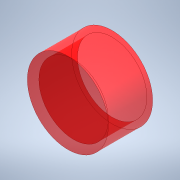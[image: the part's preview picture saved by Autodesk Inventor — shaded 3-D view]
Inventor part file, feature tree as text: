
AUTODESK INVENTOR PART (.ipt)
format: ipt  version: 2022.1 (Build 261234000, 234)  size: 387,584 bytes
history: native  units: mm
features: other x2, sketch x2, extrude x2
ambient origin geometry x8: Origin, YZ Plane, XZ Plane, XY Plane, X Axis, Y Axis, Z Axis, Center Point
bodies: Body1 (feature_tree)
feature tree (6):
  other  "plastic diffuser"
  other  "Твердое тело1"
  sketch  "Эскиз1"
  extrude  "Выдавливание1"  Depth=18.0mm
  extrude  "Выдавливание2"  Depth=21.0mm
  sketch  "Эскиз3"
